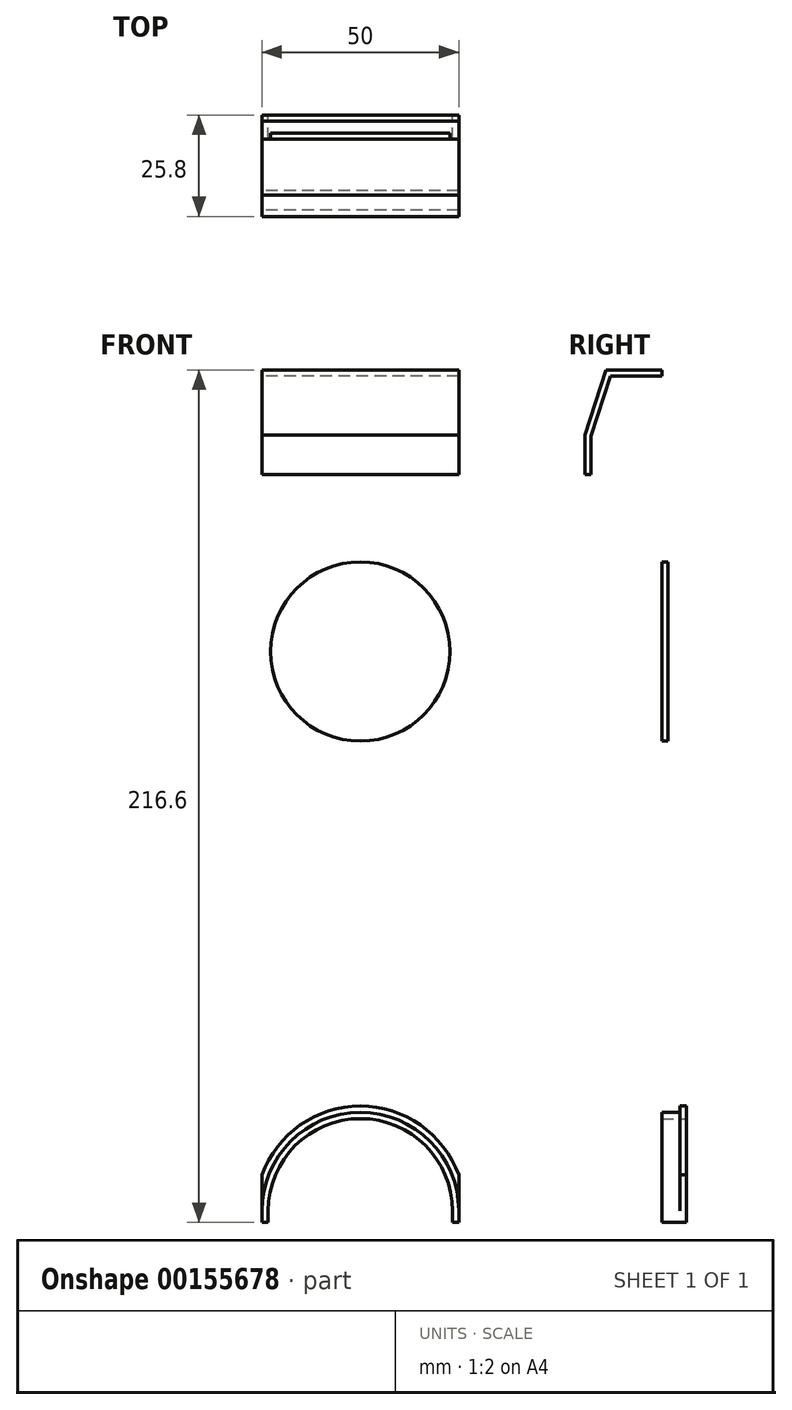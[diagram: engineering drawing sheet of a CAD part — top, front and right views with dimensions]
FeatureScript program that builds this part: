
annotation { "Feature Type Name" : "Feature", "Feature Type Description" : "" }
export const myFeature = defineFeature(function(context is Context, id is Id, definition is map)
    precondition{}
    {
        {
            var Q0;
            Q0=qCreatedBy(makeId("Right.planeOp"),FACE);
            var sketch = newSketch(context, id + "F0", { "sketchPlane" : qUnion([Q0])});
            skLineSegment(sketch, "E0", {"start": v(0, -215) * mm, "end": v(0, 0) * mm});
            skLineSegment(sketch, "E1", {"start": v(0, 0) * mm, "end": v(-13, 0) * mm});
            skLineSegment(sketch, "E2", {"start": v(-13, 0) * mm, "end": v(-18, -15.2) * mm});
            skLineSegment(sketch, "E3", {"start": v(-18, -15.2) * mm, "end": v(-18, -215) * mm});
            skLineSegment(sketch, "E4", {"start": v(-18, -215) * mm, "end": v(0, -215) * mm});
            skLineSegment(sketch, "E5.0", {"start": v(-17.75, 1.56) * mm, "end": v(-22.75, -13.64) * mm});
            skLineSegment(sketch, "E6.0", {"start": v(-19.6, -14.94) * mm, "end": v(-19.6, -215) * mm});
            skLineSegment(sketch, "E6.1", {"start": v(-14.16, 1.6) * mm, "end": v(-19.6, -14.94) * mm});
            skLineSegment(sketch, "E6.2", {"start": v(1.6, 1.6) * mm, "end": v(-14.16, 1.6) * mm});
            skLineSegment(sketch, "E6.3", {"start": v(1.6, -215) * mm, "end": v(1.6, 1.6) * mm});
            skLineSegment(sketch, "E7", {"start": v(1.6, -215) * mm, "end": v(0, -215) * mm});
            skLineSegment(sketch, "E8", {"start": v(-18, -215) * mm, "end": v(-19.6, -215) * mm});
            skLineSegment(sketch, "E9", {"start": v(-18, -24.94) * mm, "end": v(-19.6, -24.94) * mm});
            skSolve(sketch);
        }
        {
            var Q0;
            Q0=makeQuery(id+"F0.imprint","IMPRINT",FACE,{"disambiguationData":[TD([[makeQuery(id+"F0.imprint","IMPRINT",EDGE,{"derivedFrom":sQuery(id+"F0.wireOp",EDGE,"E0")}),-1.0]])]});
            extrude(context, id + "F1", {"entities" : qUnion([Q0]), "depth" : 50 * mm});
        }
        {
            var Q0;
            Q0=makeQuery(id+"F1.opExtrude","SWEPT_FACE",FACE,{"disambiguationData":[OSD([sQuery(id+"F0.wireOp",EDGE,"E6.3")])]});
            var sketch = newSketch(context, id + "F2", { "sketchPlane" : qUnion([Q0])});
            skArc(sketch, "E10", {"start": v(0, -212) * mm, "mid": v(-25, -187) * mm, "end": v(-50, -212) * mm});
            skSolve(sketch);
        }
        {
            var Q0;
            {var subQ0=sQuery(id+"F2.wireOp",EDGE,"E10");Q0=makeQuery(id+"F2.imprint","IMPRINT",FACE,{"disambiguationData":[TD([[makeQuery(id+"F2.imprint","IMPRINT",EDGE,{"derivedFrom":subQ0}),1.0]])]});}
            extrude(context, id + "F3", {"entities" : qUnion([Q0]), "operationType" : NewBodyOperationType.ADD, "depth" : 3 * mm});
        }
        {
            var Q0;
            Q0=makeQuery(id+"F3.opExtrude","CAP_FACE",FACE,{"disambiguationData":[OSD([sQuery(id+"F0.wireOp",EDGE,"E6.3"),sQuery(id+"F0.wireOp",EDGE,"E7"),sQuery(id+"F2.wireOp",EDGE,"E10")])],"isStart":false});
            var sketch = newSketch(context, id + "F4", { "sketchPlane" : qUnion([Q0])});
            skLineSegment(sketch, "E11", {"start": v(-50, -215) * mm, "end": v(-50, -182) * mm});
            skLineSegment(sketch, "E12", {"start": v(-50, -182) * mm, "end": v(0, -182) * mm});
            skLineSegment(sketch, "E13", {"start": v(0, -182) * mm, "end": v(0, -215) * mm});
            skLineSegment(sketch, "E14", {"start": v(0, -215) * mm, "end": v(-50, -215) * mm});
            skCircle(sketch, "E15", {"center": v(-25, -212) * mm, "radius": 23.4 * mm});
            skLineSegment(sketch, "E16", {"start": v(-25, -215) * mm, "end": v(-25, -212) * mm});
            skLineSegment(sketch, "E17", {"start": v(-48.4, -212) * mm, "end": v(-48.4, -215) * mm});
            skLineSegment(sketch, "E18", {"start": v(-1.6, -212) * mm, "end": v(-1.6, -215) * mm});
            skCircle(sketch, "E19", {"center": v(-25, -212) * mm, "radius": 26.6 * mm});
            skSolve(sketch);
        }
        {
            var Q0;
            {var subQ0=sQuery(id+"F4.wireOp",EDGE,"E14");Q0=makeQuery(id+"F4.imprint","IMPRINT",FACE,{"disambiguationData":[TD([[makeQuery(id+"F4.imprint","IMPRINT",EDGE,{"derivedFrom":subQ0}),1.0]])]});}
            var Q1;
            {var subQ0=sQuery(id+"F4.wireOp",EDGE,"E17");Q1=makeQuery(id+"F4.imprint","IMPRINT",FACE,{"disambiguationData":[TD([[makeQuery(id+"F4.imprint","IMPRINT",EDGE,{"derivedFrom":subQ0}),1.0]])]});}
            var Q2;
            {var subQ0=sQuery(id+"F4.wireOp",EDGE,"E18");Q2=makeQuery(id+"F4.imprint","IMPRINT",FACE,{"disambiguationData":[TD([[makeQuery(id+"F4.imprint","IMPRINT",EDGE,{"derivedFrom":subQ0}),-1.0]])]});}
            var Q3;
            Q3=makeQuery(id+"F1.opExtrude","SWEPT_FACE",FACE,{"disambiguationData":[OSD([sQuery(id+"F0.wireOp",EDGE,"E0")])]});
            extrude(context, id + "F5", {"entities" : qUnion([Q0, Q1, Q2]), "operationType" : NewBodyOperationType.REMOVE, "endBound" : BoundingType.UP_TO_SURFACE, "oppositeDirection" : true, "endBoundEntityFace" : qUnion([Q3]), "depth" : 1.6 * mm});
        }
        {
            var Q0;
            {var subQ1=makeQuery(id+"F3.opExtrude","CAP_EDGE",EDGE,{"disambiguationData":[OSD([sQuery(id+"F2.wireOp",EDGE,"E10")])],"isStart":false});Q0=makeQuery(id+"F4.imprint","IMPRINT",FACE,{"disambiguationData":[TD([[makeQuery(id+"F4.imprint","IMPRINT",EDGE,{"derivedFrom":subQ1}),-1.0]])]});}
            var Q1;
            {var subQ6=sQuery(id+"F4.wireOp",EDGE,"E17");Q1=makeQuery(id+"F4.imprint","IMPRINT",FACE,{"disambiguationData":[TD([[makeQuery(id+"F4.imprint","IMPRINT",EDGE,{"derivedFrom":subQ6}),-1.0]])]});}
            extrude(context, id + "F6", {"entities" : qUnion([Q0, Q1]), "operationType" : NewBodyOperationType.ADD, "depth" : 1.6 * mm});
        }
        {
            var Q0;
            Q0=makeQuery(id+"F1.opExtrude","SWEPT_FACE",FACE,{"disambiguationData":[OSD([sQuery(id+"F0.wireOp",EDGE,"E6.3")])]});
            var sketch = newSketch(context, id + "F7", { "sketchPlane" : qUnion([Q0])});
            skLineSegment(sketch, "E20", {"start": v(-25, 1.6) * mm, "end": v(-25, -259.64) * mm});
            skCircle(sketch, "E21", {"center": v(-25, -164.22) * mm, "radius": 22.77 * mm});
            skCircle(sketch, "E22", {"center": v(-25, -117.07) * mm, "radius": 22.77 * mm});
            skCircle(sketch, "E23", {"center": v(-25, -69.92) * mm, "radius": 22.77 * mm});
            skCircle(sketch, "E24", {"center": v(-25, -22.77) * mm, "radius": 22.77 * mm});
            skSolve(sketch);
        }
        {
            var Q0;
            {var subQ0=sQuery(id+"F7.wireOp",EDGE,"E21");var subQ1=sQuery(id+"F7.wireOp",EDGE,"E20");var subQ2=makeQuery(id+"F7.imprint","INTERSECT",VERTEX,{"derivedFrom":[subQ1,subQ0]});Q0=makeQuery(id+"F7.imprint","IMPRINT",FACE,{"disambiguationData":[TD([[makeQuery(id+"F7.imprint","IMPRINT",EDGE,{"disambiguationData":[TD([[subQ2,-1.0]])],"derivedFrom":subQ1}),-1.0]])]});}
            var Q1;
            {var subQ0=sQuery(id+"F7.wireOp",EDGE,"E21");var subQ1=sQuery(id+"F7.wireOp",EDGE,"E20");var subQ2=makeQuery(id+"F7.imprint","INTERSECT",VERTEX,{"derivedFrom":[subQ1,subQ0]});Q1=makeQuery(id+"F7.imprint","IMPRINT",FACE,{"disambiguationData":[TD([[makeQuery(id+"F7.imprint","IMPRINT",EDGE,{"disambiguationData":[TD([[subQ2,-1.0]])],"derivedFrom":subQ1}),1.0]])]});}
            var Q2;
            {var subQ0=sQuery(id+"F7.wireOp",EDGE,"E22");var subQ1=sQuery(id+"F7.wireOp",EDGE,"E20");var subQ2=makeQuery(id+"F7.imprint","INTERSECT",VERTEX,{"disambiguationData":[OD(0.0)],"derivedFrom":[subQ1,subQ0]});Q2=makeQuery(id+"F7.imprint","IMPRINT",FACE,{"disambiguationData":[TD([[makeQuery(id+"F7.imprint","IMPRINT",EDGE,{"disambiguationData":[TD([[subQ2,-1.0]])],"derivedFrom":subQ1}),1.0]])]});}
            var Q3;
            {var subQ0=sQuery(id+"F7.wireOp",EDGE,"E22");var subQ1=sQuery(id+"F7.wireOp",EDGE,"E20");var subQ2=makeQuery(id+"F7.imprint","INTERSECT",VERTEX,{"disambiguationData":[OD(0.0)],"derivedFrom":[subQ1,subQ0]});Q3=makeQuery(id+"F7.imprint","IMPRINT",FACE,{"disambiguationData":[TD([[makeQuery(id+"F7.imprint","IMPRINT",EDGE,{"disambiguationData":[TD([[subQ2,-1.0]])],"derivedFrom":subQ1}),-1.0]])]});}
            var Q4;
            {var subQ0=sQuery(id+"F7.wireOp",EDGE,"E23");var subQ1=sQuery(id+"F7.wireOp",EDGE,"E20");var subQ2=makeQuery(id+"F7.imprint","INTERSECT",VERTEX,{"disambiguationData":[OD(0.0)],"derivedFrom":[subQ1,subQ0]});Q4=makeQuery(id+"F7.imprint","IMPRINT",FACE,{"disambiguationData":[TD([[makeQuery(id+"F7.imprint","IMPRINT",EDGE,{"disambiguationData":[TD([[subQ2,-1.0]])],"derivedFrom":subQ1}),-1.0]])]});}
            var Q5;
            {var subQ0=sQuery(id+"F7.wireOp",EDGE,"E23");var subQ1=sQuery(id+"F7.wireOp",EDGE,"E20");var subQ2=makeQuery(id+"F7.imprint","INTERSECT",VERTEX,{"disambiguationData":[OD(0.0)],"derivedFrom":[subQ1,subQ0]});Q5=makeQuery(id+"F7.imprint","IMPRINT",FACE,{"disambiguationData":[TD([[makeQuery(id+"F7.imprint","IMPRINT",EDGE,{"disambiguationData":[TD([[subQ2,-1.0]])],"derivedFrom":subQ1}),1.0]])]});}
            var Q6;
            {var subQ0=sQuery(id+"F7.wireOp",EDGE,"E20");var subQ3=sQuery(id+"F7.wireOp",EDGE,"E24");var subQ4=makeQuery(id+"F7.imprint","INTERSECT",VERTEX,{"derivedFrom":[subQ0,subQ3]});Q6=makeQuery(id+"F7.imprint","IMPRINT",FACE,{"disambiguationData":[TD([[makeQuery(id+"F7.imprint","IMPRINT",EDGE,{"disambiguationData":[TD([[subQ4,1.0]])],"derivedFrom":subQ0}),1.0]])]});}
            var Q7;
            {var subQ0=sQuery(id+"F7.wireOp",EDGE,"E20");var subQ3=sQuery(id+"F7.wireOp",EDGE,"E24");var subQ4=makeQuery(id+"F7.imprint","INTERSECT",VERTEX,{"derivedFrom":[subQ0,subQ3]});Q7=makeQuery(id+"F7.imprint","IMPRINT",FACE,{"disambiguationData":[TD([[makeQuery(id+"F7.imprint","IMPRINT",EDGE,{"disambiguationData":[TD([[subQ4,1.0]])],"derivedFrom":subQ0}),-1.0]])]});}
            var Q8;
            Q8=makeQuery(id+"F1.opExtrude","SWEPT_FACE",FACE,{"disambiguationData":[OSD([sQuery(id+"F0.wireOp",EDGE,"E0")])]});
            extrude(context, id + "F8", {"entities" : qUnion([Q0, Q1, Q2, Q3, Q4, Q5, Q6, Q7]), "operationType" : NewBodyOperationType.REMOVE, "endBound" : BoundingType.UP_TO_SURFACE, "oppositeDirection" : true, "endBoundEntityFace" : qUnion([Q8]), "depth" : 25 * mm});
        }
    });
